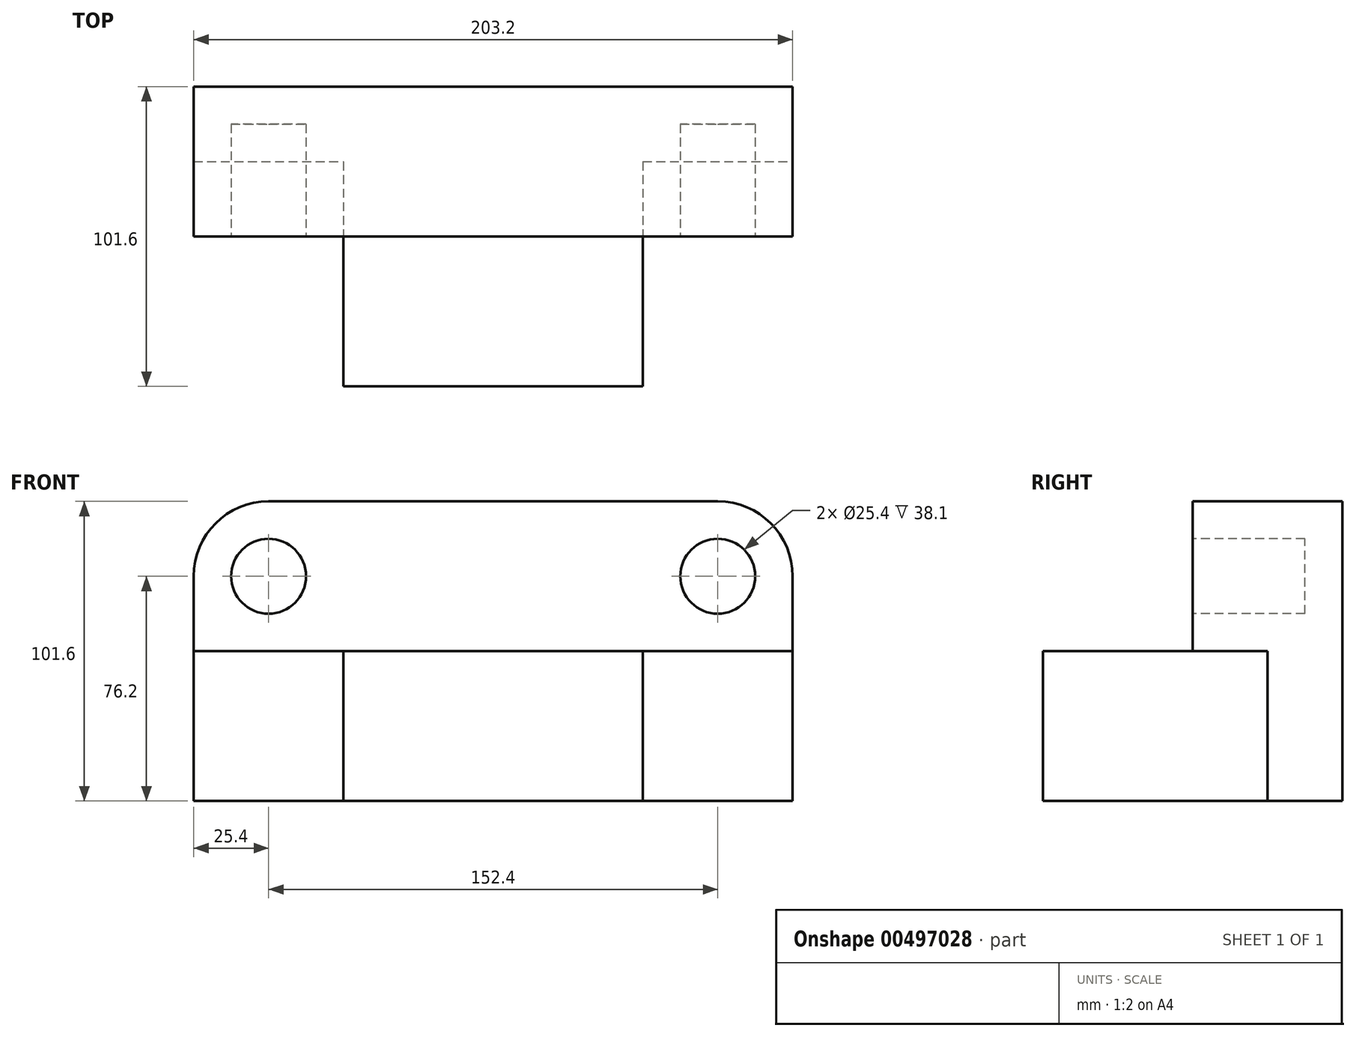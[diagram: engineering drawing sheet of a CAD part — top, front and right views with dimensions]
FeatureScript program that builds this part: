
annotation { "Feature Type Name" : "Feature", "Feature Type Description" : "" }
export const myFeature = defineFeature(function(context is Context, id is Id, definition is map)
    precondition{}
    {
        {
            var Q0;
            Q0=qCreatedBy(makeId("Front.planeOp"),FACE);
            var sketch = newSketch(context, id + "F0", { "sketchPlane" : qUnion([Q0])});
            skLineSegment(sketch, "E0.bottom", {"start": v(0, 0) * mm, "end": v(203.2, 0) * mm});
            skLineSegment(sketch, "E0.top", {"start": v(0, 101.6) * mm, "end": v(203.2, 101.6) * mm});
            skLineSegment(sketch, "E0.left", {"start": v(0, 0) * mm, "end": v(0, 101.6) * mm});
            skLineSegment(sketch, "E0.right", {"start": v(203.2, 0) * mm, "end": v(203.2, 101.6) * mm});
            skSolve(sketch);
        }
        {
            var Q0;
            Q0=makeQuery(id+"F0.imprint","IMPRINT",FACE,{"disambiguationData":[TD([[makeQuery(id+"F0.imprint","IMPRINT",EDGE,{"derivedFrom":sQuery(id+"F0.wireOp",EDGE,"E0.bottom")}),1.0]])]});
            extrude(context, id + "F1", {"entities" : qUnion([Q0]), "depth" : 101.6 * mm});
        }
        {
            var Q0;
            Q0=makeQuery(id+"F1.opExtrude","CAP_FACE",FACE,{"disambiguationData":[OSD([sQuery(id+"F0.wireOp",EDGE,"E0.bottom"),sQuery(id+"F0.wireOp",EDGE,"E0.top"),sQuery(id+"F0.wireOp",EDGE,"E0.left"),sQuery(id+"F0.wireOp",EDGE,"E0.right")])],"isStart":false});
            var sketch = newSketch(context, id + "F2", { "sketchPlane" : qUnion([Q0])});
            skLineSegment(sketch, "E1", {"start": v(50.8, 0) * mm, "end": v(50.8, 50.8) * mm});
            skLineSegment(sketch, "E2", {"start": v(50.8, 50.8) * mm, "end": v(0, 50.8) * mm});
            skLineSegment(sketch, "E3", {"start": v(152.4, 0) * mm, "end": v(152.4, 50.8) * mm});
            skLineSegment(sketch, "E4", {"start": v(152.4, 50.8) * mm, "end": v(203.2, 50.8) * mm});
            skSolve(sketch);
        }
        {
            var Q0;
            Q0 = qSketchRegion(id + "F2", true);
            var Q1;
            {var subQ0=sQuery(id+"F2.wireOp",EDGE,"E1");Q1=makeQuery(id+"F2.imprint","IMPRINT",FACE,{"disambiguationData":[TD([[makeQuery(id+"F2.imprint","IMPRINT",EDGE,{"derivedFrom":subQ0}),1.0]])]});}
            var Q2;
            {var subQ0=sQuery(id+"F2.wireOp",EDGE,"E3");Q2=makeQuery(id+"F2.imprint","IMPRINT",FACE,{"disambiguationData":[TD([[makeQuery(id+"F2.imprint","IMPRINT",EDGE,{"derivedFrom":subQ0}),-1.0]])]});}
            extrude(context, id + "F3", {"entities" : qUnion([Q0, Q1, Q2]), "operationType" : NewBodyOperationType.REMOVE, "oppositeDirection" : true, "depth" : 76.2 * mm});
        }
        {
            var Q0;
            Q0=makeQuery(id+"F1.opExtrude","CAP_FACE",FACE,{"disambiguationData":[OSD([sQuery(id+"F0.wireOp",EDGE,"E0.bottom"),sQuery(id+"F0.wireOp",EDGE,"E0.top"),sQuery(id+"F0.wireOp",EDGE,"E0.left"),sQuery(id+"F0.wireOp",EDGE,"E0.right")])],"isStart":false});
            var sketch = newSketch(context, id + "F4", { "sketchPlane" : qUnion([Q0])});
            skLineSegment(sketch, "E5", {"start": v(50.8, 50.8) * mm, "end": v(152.4, 50.8) * mm});
            skSolve(sketch);
        }
        {
            var Q0;
            Q0=makeQuery(id+"F4.imprint","IMPRINT",FACE,{"disambiguationData":[TD([[makeQuery(id+"F4.imprint","IMPRINT",EDGE,{"derivedFrom":sQuery(id+"F4.wireOp",EDGE,"E5")}),1.0]])]});
            extrude(context, id + "F5", {"entities" : qUnion([Q0]), "operationType" : NewBodyOperationType.REMOVE, "oppositeDirection" : true, "depth" : 50.8 * mm});
        }
        {
            var Q0;
            Q0=makeQuery(id+"F1.opExtrude","SWEPT_EDGE",EDGE,{"disambiguationData":[OSD([sQuery(id+"F0.wireOp",EDGE,"E0.top"),sQuery(id+"F0.wireOp",EDGE,"E0.right")])]});
            var Q1;
            Q1=makeQuery(id+"F1.opExtrude","SWEPT_EDGE",EDGE,{"disambiguationData":[OSD([sQuery(id+"F0.wireOp",EDGE,"E0.top"),sQuery(id+"F0.wireOp",EDGE,"E0.left")])]});
            fillet(context, id + "F6", {"entities" : qUnion([Q0, Q1]), "radius" : 25.4 * mm, "tangentPropagation" : true, "allowEdgeOverflow" : false});
        }
        {
            var Q0;
            Q0=makeQuery(id+"F5.boolean.opBoolean","COPY",FACE,{"derivedFrom":makeQuery(id+"F5.opExtrude","CAP_FACE",FACE,{"disambiguationData":[OSD([sQuery(id+"F0.wireOp",EDGE,"E0.top"),sQuery(id+"F0.wireOp",EDGE,"E0.left"),sQuery(id+"F0.wireOp",EDGE,"E0.right"),sQuery(id+"F2.wireOp",EDGE,"E2"),sQuery(id+"F2.wireOp",EDGE,"E4"),sQuery(id+"F4.wireOp",EDGE,"E5")])],"isStart":false})});
            var sketch = newSketch(context, id + "F7", { "sketchPlane" : qUnion([Q0])});
            skCircle(sketch, "E6", {"center": v(25.4, 76.2) * mm, "radius": 12.7 * mm});
            skCircle(sketch, "E7", {"center": v(177.8, 76.2) * mm, "radius": 12.7 * mm});
            skSolve(sketch);
        }
        {
            var Q0;
            Q0 = qSketchRegion(id + "F7", true);
            extrude(context, id + "F8", {"entities" : qUnion([Q0]), "operationType" : NewBodyOperationType.REMOVE, "oppositeDirection" : true, "depth" : 38.1 * mm});
        }
    });
